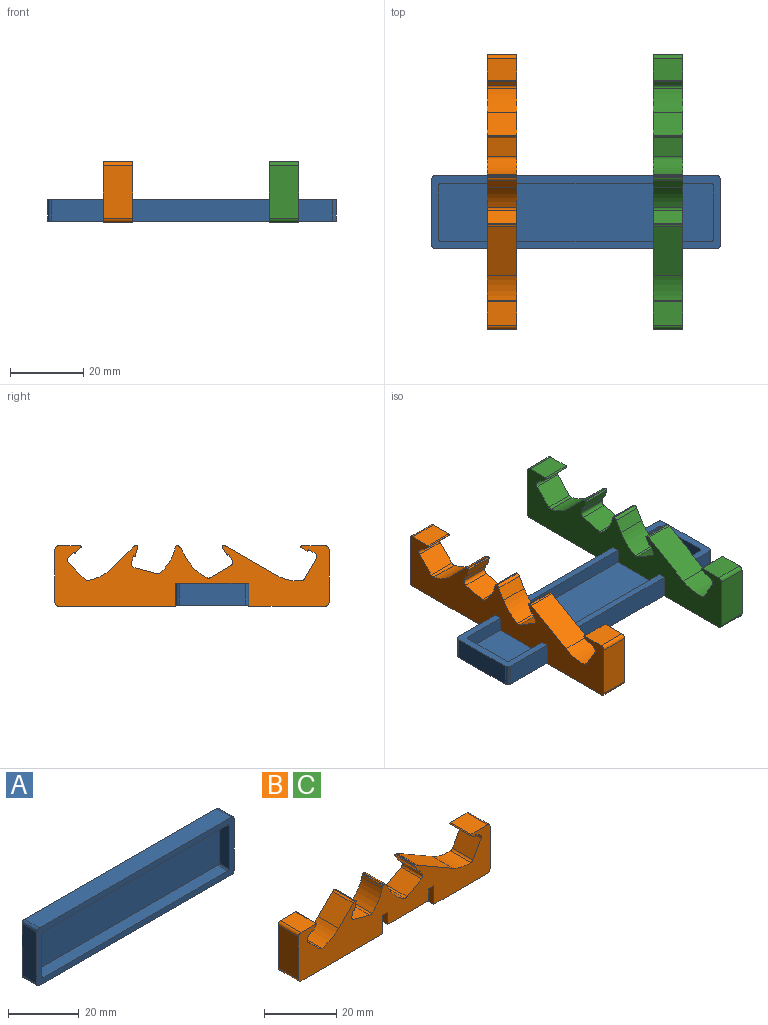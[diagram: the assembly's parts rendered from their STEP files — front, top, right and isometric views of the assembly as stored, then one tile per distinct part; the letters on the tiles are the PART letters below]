
ASSEMBLY  parts=3 mates=4
PART A: 19 faces, bbox 79x6x20 mm
  f0: plane 18x6mm, normal (-1,0,0), area 108mm2, adj f4,f5,f11,f14
  f1: plane 77x6mm, normal (0,0,-1), area 462mm2, adj f4,f5,f11,f12
  f2: plane 18x6mm, normal (1,0,0), area 108mm2, adj f4,f5,f12,f13
  f3: plane 77x6mm, normal (0,0,1), area 462mm2, adj f4,f5,f13,f14
  f4: plane 79x20mm, normal (0,-1,0), area 379.4mm2, adj f0,f1,f2,f3,f6,f7,f8,f9
  f5: plane 79x20mm, normal (0,1,0), area 1579.1mm2, adj f0,f1,f2,f3,f11,f12,f13,f14
  f6: plane 15x4mm, normal (1,0,0), area 60mm2, adj f4,f10,f16,f18
  f7: plane 74x4mm, normal (0,0,1), area 296mm2, adj f4,f10,f17,f18
  f8: plane 15x4mm, normal (-1,0,0), area 60mm2, adj f4,f10,f15,f17
  f9: plane 74x4mm, normal (0,0,-1), area 296mm2, adj f4,f10,f15,f16
  f10: plane 75x16mm, normal (0,-1,0), area 1199.8mm2, adj f6,f7,f8,f9,f15,f16,f17,f18
  f11: cylinder r=1mm len=6mm, axis (0,1,0), area 9.4mm2, adj f0,f1,f4,f5
  f12: cylinder r=1mm len=6mm, axis (0,-1,0), area 9.4mm2, adj f1,f2,f4,f5
  f13: cylinder r=1mm len=6mm, axis (0,1,0), area 9.4mm2, adj f2,f3,f4,f5
  f14: cylinder r=1mm len=6mm, axis (0,-1,0), area 9.4mm2, adj f0,f3,f4,f5
  f15: cylinder r=0.5mm len=4mm, axis (0,-1,0), area 3.1mm2, adj f4,f8,f9,f10
  f16: cylinder r=0.5mm len=4mm, axis (0,1,0), area 3.1mm2, adj f4,f6,f9,f10
  f17: cylinder r=0.5mm len=4mm, axis (0,1,0), area 3.1mm2, adj f4,f7,f8,f10
  f18: cylinder r=0.5mm len=4mm, axis (0,-1,0), area 3.1mm2, adj f4,f6,f7,f10
PART B: 66 faces, bbox 75x8x16.5 mm
  f0: cylinder r=12.5mm len=8mm, axis (0,1,0), area 60.1mm2, adj f1,f40,f41,f56
  f1: plane 8x3.2mm, normal (0.87,0,0.5), area 29.6mm2, adj f0,f40,f41,f42
  f2: plane 8x0.23mm, normal (0,0,1), area 1.8mm2, adj f40,f41,f42,f57
  f3: plane 8x0.95mm, normal (-0.97,0,0.26), area 7.9mm2, adj f4,f40,f41,f57
  f4: cylinder r=12.5mm len=8mm, axis (0,1,0), area 60.1mm2, adj f3,f40,f41,f43
  f5: plane 8x6.27mm, normal (0.26,0,0.97), area 51.9mm2, adj f40,f41,f43,f44
  f6: plane 8x1.93mm, normal (0.97,0,-0.26), area 16mm2, adj f7,f40,f41,f44
  f7: plane 8x0.24mm, normal (-0.26,0,-0.97), area 2mm2, adj f6,f40,f41,f58
  f8: plane 8x2.34mm, normal (0.97,0,-0.26), area 19.4mm2, adj f40,f41,f58,f59
  f9: plane 8x0.26mm, normal (0,0,1), area 2.1mm2, adj f40,f41,f45,f59
  f10: plane 8x5.72mm, normal (-0.71,0,0.71), area 64.7mm2, adj f11,f40,f41,f45
  f11: cylinder r=12.5mm len=8mm, axis (0,1,0), area 60.1mm2, adj f10,f40,f41,f46
  f12: plane 8x4.59mm, normal (0.71,0,0.71), area 51.9mm2, adj f40,f41,f46,f47
  f13: plane 8x1.41mm, normal (0.71,0,-0.71), area 16mm2, adj f14,f40,f41,f47
  f14: plane 8x0.18mm, normal (-0.71,0,-0.71), area 2mm2, adj f13,f40,f41,f60
  f15: plane 8x1.52mm, normal (0.71,0,-0.71), area 17.2mm2, adj f40,f41,f60,f61
  f16: plane 8x5.95mm, normal (0,0,1), area 47.6mm2, adj f40,f41,f48,f61
  f17: plane 14.5x8mm, normal (-1,0,0), area 116mm2, adj f40,f41,f48,f49
  f18: plane 32.05x8mm, normal (0,0,-1), area 256.4mm2, adj f19,f40,f41,f49
  f19: plane 8x6.25mm, normal (1,0,0), area 50mm2, adj f18,f20,f40,f41
  f20: plane 8x2mm, normal (0,0,-1), area 16mm2, adj f19,f21,f40,f41
  f21: plane 8x4mm, normal (-1,0,0), area 32mm2, adj f20,f22,f40,f41
  f22: plane 16x8mm, normal (0,0,-1), area 128mm2, adj f21,f23,f40,f41
  f23: plane 8x4mm, normal (1,0,0), area 32mm2, adj f22,f24,f40,f41
  f24: plane 8x2mm, normal (0,0,-1), area 16mm2, adj f23,f25,f40,f41
  f25: plane 8x6.25mm, normal (-1,0,0), area 50mm2, adj f24,f26,f40,f41
  f26: plane 20.95x8mm, normal (0,0,-1), area 167.6mm2, adj f25,f40,f41,f50
  f27: plane 14.5x8mm, normal (1,0,0), area 116mm2, adj f40,f41,f50,f51
  f28: plane 8x6.47mm, normal (0,0,1), area 51.8mm2, adj f40,f41,f51,f62
  f29: plane 8x1.57mm, normal (-0.5,0,-0.87), area 14.5mm2, adj f40,f41,f62,f63
  f30: plane 8x0.22mm, normal (0.87,0,-0.5), area 2mm2, adj f31,f40,f41,f63
  f31: plane 8x1.73mm, normal (-0.5,0,-0.87), area 16mm2, adj f30,f40,f41,f52
  f32: plane 8x5.62mm, normal (-0.87,0,0.5), area 51.9mm2, adj f40,f41,f52,f53
  f33: cylinder r=12.5mm len=8mm, axis (0,1,0), area 60.1mm2, adj f34,f40,f41,f53
  f34: plane 13.47x8mm, normal (0.5,0,0.87), area 124.4mm2, adj f33,f40,f41,f54
  f35: plane 8x0.3mm, normal (0,0,1), area 2.4mm2, adj f40,f41,f54,f64
  f36: plane 8x2.01mm, normal (-0.87,0,-0.5), area 18.5mm2, adj f40,f41,f64,f65
  f37: plane 8x0.22mm, normal (0.5,0,-0.87), area 2mm2, adj f38,f40,f41,f65
  f38: plane 8x1.73mm, normal (-0.87,0,-0.5), area 16mm2, adj f37,f40,f41,f55
  f39: plane 8x5.62mm, normal (-0.5,0,0.87), area 51.9mm2, adj f40,f41,f55,f56
  f40: plane 75x16.5mm, normal (0,-1,0), area 774.9mm2, adj f0,f1,f2,f3,f4,f5,f6,f7
  f41: plane 75x16.5mm, normal (0,1,0), area 774.9mm2, adj f0,f1,f2,f3,f4,f5,f6,f7
  f42: cylinder r=1mm len=8mm, axis (0,1,0), area 8.4mm2, adj f1,f2,f40,f41
  f43: cylinder r=1mm len=8mm, axis (0,1,0), area 7.8mm2, adj f4,f5,f40,f41
  f44: cylinder r=1mm len=8mm, axis (0,-1,0), area 12.6mm2, adj f5,f6,f40,f41
  f45: cylinder r=1mm len=8mm, axis (0,-1,0), area 6.3mm2, adj f9,f10,f40,f41
  f46: cylinder r=1mm len=8mm, axis (0,1,0), area 7.8mm2, adj f11,f12,f40,f41
  f47: cylinder r=1mm len=8mm, axis (0,-1,0), area 12.6mm2, adj f12,f13,f40,f41
  f48: cylinder r=1mm len=8mm, axis (0,-1,0), area 12.6mm2, adj f16,f17,f40,f41
  f49: cylinder r=1mm len=8mm, axis (0,1,0), area 12.6mm2, adj f17,f18,f40,f41
  f50: cylinder r=1mm len=8mm, axis (0,1,0), area 12.6mm2, adj f26,f27,f40,f41
  f51: cylinder r=1mm len=8mm, axis (0,1,0), area 12.6mm2, adj f27,f28,f40,f41
  f52: cylinder r=1mm len=8mm, axis (0,-1,0), area 12.6mm2, adj f31,f32,f40,f41
  f53: cylinder r=1mm len=8mm, axis (0,1,0), area 7.8mm2, adj f32,f33,f40,f41
  f54: cylinder r=1mm len=8mm, axis (0,1,0), area 4.2mm2, adj f34,f35,f40,f41
  f55: cylinder r=1mm len=8mm, axis (0,-1,0), area 12.6mm2, adj f38,f39,f40,f41
  f56: cylinder r=1mm len=8mm, axis (0,1,0), area 7.8mm2, adj f0,f39,f40,f41
  f57: cylinder r=0.25mm len=8mm, axis (0,-1,0), area 2.6mm2, adj f2,f3,f40,f41
  f58: cylinder r=0.25mm len=8mm, axis (0,1,0), area 3.1mm2, adj f7,f8,f40,f41
  f59: cylinder r=0.25mm len=8mm, axis (0,1,0), area 3.7mm2, adj f8,f9,f40,f41
  f60: cylinder r=0.25mm len=8mm, axis (0,1,0), area 3.1mm2, adj f14,f15,f40,f41
  f61: cylinder r=0.25mm len=8mm, axis (0,1,0), area 4.7mm2, adj f15,f16,f40,f41
  f62: cylinder r=0.25mm len=8mm, axis (0,1,0), area 5.2mm2, adj f28,f29,f40,f41
  f63: cylinder r=0.25mm len=8mm, axis (0,1,0), area 3.1mm2, adj f29,f30,f40,f41
  f64: cylinder r=0.25mm len=8mm, axis (0,-1,0), area 4.2mm2, adj f35,f36,f40,f41
  f65: cylinder r=0.25mm len=8mm, axis (0,1,0), area 3.1mm2, adj f36,f37,f40,f41
PART C: same geometry as B
PLACE A rot(axis=(-1,0,0),90deg) t=(-17.62,-27.23,-25.51)mm fixed
PLACE B rot(axis=(0,0,-1),90deg) t=(-37.89,-21.68,-25.76)mm
PLACE C rot(axis=(0,0,-1),90deg) t=(7.58,-21.68,-25.76)mm
MATE planar A.f10 <-> C.f22  axis (0,0,1) through (-17.62,-27.23,-23.51)mm
MATE planar A.f7 <-> C.f23  axis (0,1,0) through (-17.62,-35.23,-21.51)mm
MATE planar A.f10 <-> B.f22  axis (0,0,1) through (-17.62,-27.23,-23.51)mm
MATE planar A.f7 <-> B.f23  axis (0,1,0) through (-17.62,-35.23,-21.51)mm
